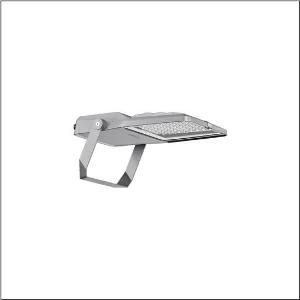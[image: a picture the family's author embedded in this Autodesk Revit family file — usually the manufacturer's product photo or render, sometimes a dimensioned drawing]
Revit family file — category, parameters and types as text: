
# Revit family: floodlight_fl_21_iq_mini___pl43_5xa7771c4a1a_6230
name_source: partatom
category: Lighting Fixtures
units: mm (PartAtom-declared; Revit-internal decimal feet)

## family parameters
Cut with Voids When Loaded = No
Host = Face
Light Source = No
Part Type = Normal
Room Calculation Point = No
Round Connector Dimension = Use Diameter
Shared = No

## types (1)
- --- (1 x LED, 13050 lm, 87.2 W, 4000K)
    Apparent Load = 87 VA
    CIE Flux Codes = 27 78 99 100 100
    Color Rendering = 70
    Color Temperature = 4000K
    Default Elevation = 1800 mm
    Description = Floodlight FL 21 iQ mini, floodlight, primary light control with lens, of PMMA, primary optical cover: protective disc, of toughened safety glass, transparent, light distribution: PL43, light emission: direct distribution, installation type: surface-mounted, LED, High Power LED, rated luminous flux: 13.050lm, luminous efficacy: 150lm/W, light colour: 740, colour temperature: 4000K, control: Auto-Match, Temp-Guard, Lumen-Switch, Night-Set, Smart-Wire, Light-Fading, Desk-Remote (wireless, voltage-free reading and setting of iQ features in the workshop via application-optimized NFC function/RFID function), optimised constant luminous flux control (CLO 2.0), with terminal, 6-pole, mains connection: 220..240V, AC, 50/60Hz, start of lifetime: 87W, end of service life: 92W, reduction: 40W, luminaire housing, of diecast aluminium, powder-coated, Siteco® metallic grey (DB 702S), corrosivity category C5 mid according to DIN EN ISO 12944, sealing non-destructively replaceable, mounting bracket, of steel, galvanised, powder-coated, Siteco® metallic grey (DB 702S), protection rating (complete): IP66, insulation class (complete): insulation class II (safety insulation), certification: CE, ENEC, VDE, protection symbol: D, impact resistance: IK08, permissible operating ambient temperature: -40..+40°C, permissible operating ambient temperature for outdoor applications: -40..+50°C, standard: DIN EN 12944, LABS conformity tested according to VDMA 24364:2018-05, packaging unit: 1 piece

Light Distribution: PL43
    Height = 70 mm
    Lamp = 1 x LED
    Lamp Light Flux = 13050 lm
    Lamp Power = 87.2 W
    Lamp count = 1
    Length = 485 mm
    Luminous efficacy = 150 lm/W
    Manufacturer = Siteco
    ModVariant = No
    Model = 5XA7771C4A1A
    Number of Poles = 1
    OnlyDefault = Yes
    Power Factor = 1
    Product Name = Floodlight FL 21 iQ mini | PL43
    Product group = floodlight | pylon annexe
    ProductGroupID = 6200
    Protection Class = Protection class II
    Protection Degree = IP 66
    RLX_Detail_Level = 1
    RLX_Emergency_Light_Flux = 0 lm
    RLX_Emergency_Type = 0
    RLX_Emergency_Type_DB = No
    RlxData = <blob elided: 96205 chars, md5=9ee1d894>
    Socket = socket
    Standby Power = 0 W
    System Light Flux = 13050 lm
    System Power = 87 W
    Type Comments = factory setting: luminous flux: 100 % | dim-lin: 254 | 456 mA
    Type Image = l_1006845.jpg
    URL = http://relux.com
    VarID = @adj_112093
    Voltage = 0 V
    Weight = 0.00 kg
    Width = 337 mm

## geometry (parser evidence)
native form markers: Blend x4, Sweep x11
no freeform markers — native parametric forms only
